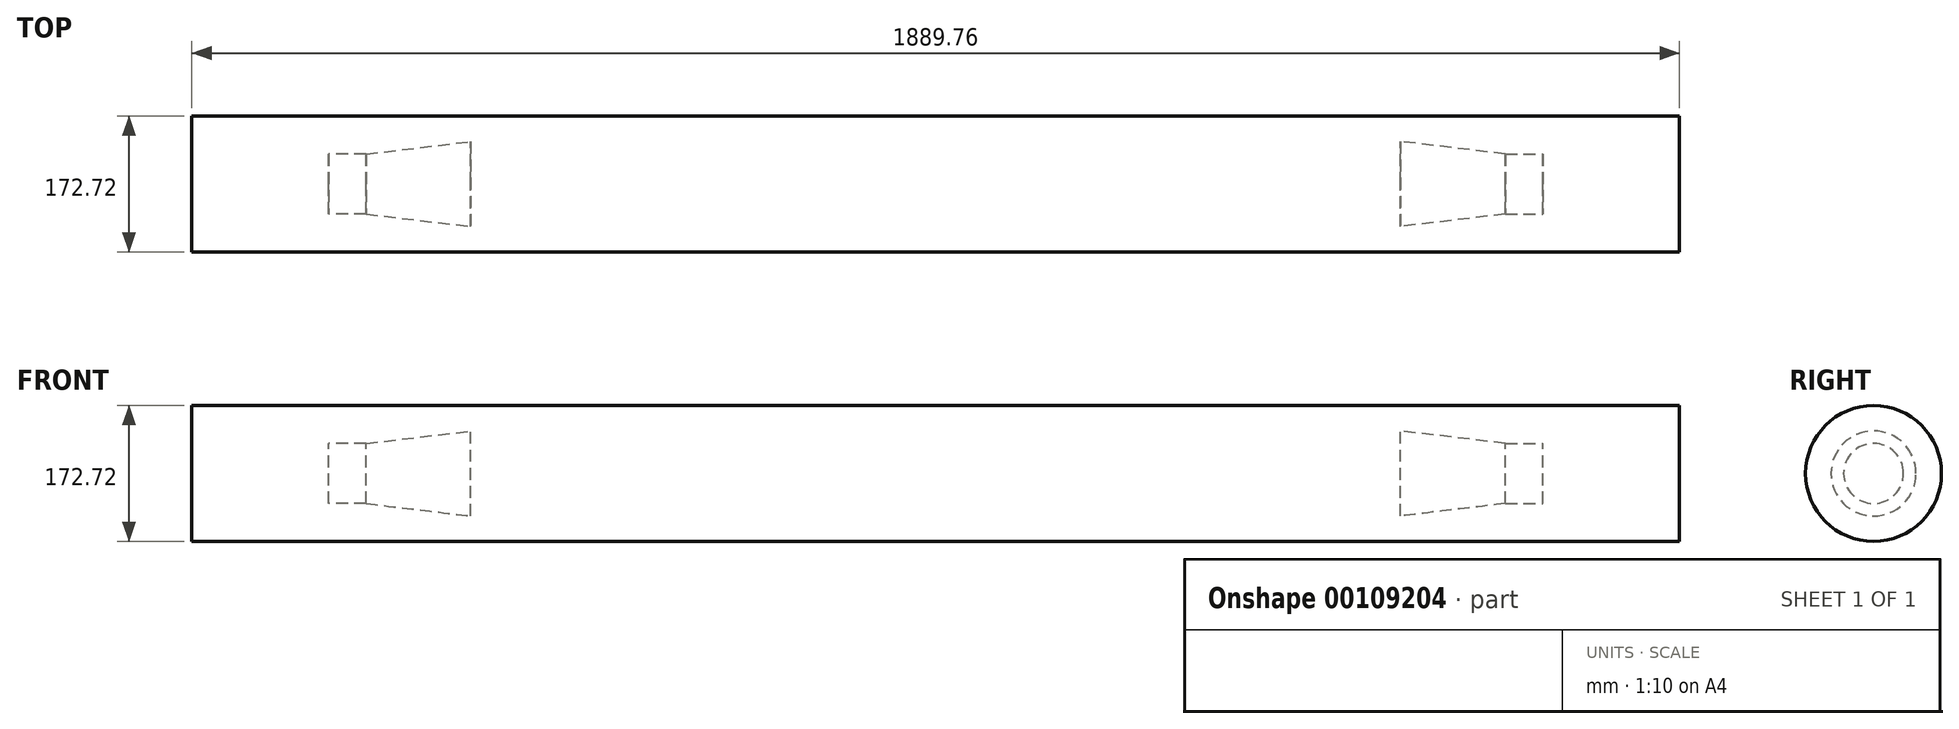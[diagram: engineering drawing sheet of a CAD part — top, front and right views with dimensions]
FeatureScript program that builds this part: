
annotation { "Feature Type Name" : "Feature", "Feature Type Description" : "" }
export const myFeature = defineFeature(function(context is Context, id is Id, definition is map)
    precondition{}
    {
        {
            var Q0;
            Q0=qCreatedBy(makeId("Right.planeOp"),FACE);
            var sketch = newSketch(context, id + "F0", { "sketchPlane" : qUnion([Q0])});
            skCircle(sketch, "E0", {"center": v(0, 0) * mm, "radius": 53.97 * mm});
            skSolve(sketch);
        }
        {
            var Q0;
            Q0=qSketchRegion(id+"F0",true);
            extrude(context, id + "F1", {"entities" : qUnion([Q0]), "endBound" : BoundingType.SYMMETRIC, "depth" : 1181.1 * mm});
        }
        {
            var Q0;
            Q0=makeQuery(id+"F1.opExtrude","CAP_FACE",FACE,{"disambiguationData":[OSD([sQuery(id+"F0.wireOp",EDGE,"E0")])],"isStart":false});
            cPlane(context, id + "F2", {"entities" : qUnion([Q0]), "cplaneType" : CPlaneType.OFFSET, "offset" : 180.85 * mm, "width" : 152.4 * mm, "height" : 152.4 * mm});
        }
        {
            var Q0;
            Q0=qCreatedBy(id+"F2.planeOp",FACE);
            var sketch = newSketch(context, id + "F3", { "sketchPlane" : qUnion([Q0])});
            skCircle(sketch, "E1", {"center": v(0, 0) * mm, "radius": 38.1 * mm});
            skSolve(sketch);
        }
        {
            var Q0;
            Q0=qSketchRegion(id+"F3",true);
            extrude(context, id + "F4", {"entities" : qUnion([Q0]), "oppositeDirection" : true, "depth" : 47.75 * mm});
        }
        {
            var Q0;
            Q0=makeQuery(id+"F4.opExtrude","SWEPT_BODY",BODY,{"disambiguationData":[OSD([sQuery(id+"F3.wireOp",EDGE,"E1")])]});
            var Q1;
            Q1=qCreatedBy(makeId("Right.planeOp"),FACE);
            mirror(context, id + "F5", {"entities" : qUnion([Q0]), "mirrorPlane" : qUnion([Q1])});
        }
        {
            var Q0;
            Q0=makeQuery(id+"F1.opExtrude","CAP_FACE",FACE,{"disambiguationData":[OSD([sQuery(id+"F0.wireOp",EDGE,"E0")])],"isStart":false});
            var Q1;
            Q1=makeQuery(id+"F4.opExtrude","CAP_FACE",FACE,{"disambiguationData":[OSD([sQuery(id+"F3.wireOp",EDGE,"E1")])],"isStart":false});
            loft(context, id + "F6", {"sheetProfilesArray" : [{ "sheetProfileEntities" : qUnion([Q0]) }, { "sheetProfileEntities" : qUnion([Q1]) }]});
        }
        {
            var Q0;
            Q0=makeQuery(id+"F1.opExtrude","CAP_FACE",FACE,{"disambiguationData":[OSD([sQuery(id+"F0.wireOp",EDGE,"E0")])],"isStart":true});
            var Q1;
            Q1=makeQuery(id+"F5.opPattern","COPY",FACE,{"derivedFrom":makeQuery(id+"F4.opExtrude","CAP_FACE",FACE,{"disambiguationData":[OSD([sQuery(id+"F3.wireOp",EDGE,"E1")])],"isStart":false}),"instanceName":"1"});
            loft(context, id + "F7", {"sheetProfilesArray" : [{ "sheetProfileEntities" : qUnion([Q0]) }, { "sheetProfileEntities" : qUnion([Q1]) }]});
        }
        {
            var Q0;
            Q0=makeQuery(id+"F1.opExtrude","SWEPT_BODY",BODY,{"disambiguationData":[OSD([sQuery(id+"F0.wireOp",EDGE,"E0")])]});
            var Q1;
            Q1=qCreatedBy(makeId("Origin.pointOp"),VERTEX);
            transform(context, id + "F8", {"entities" : qUnion([Q0]), "transformType" : TransformType.SCALE_UNIFORMLY, "scale" : 1.6, "scalePoint" : qUnion([Q1]), "makeCopy" : false});
        }
    });
